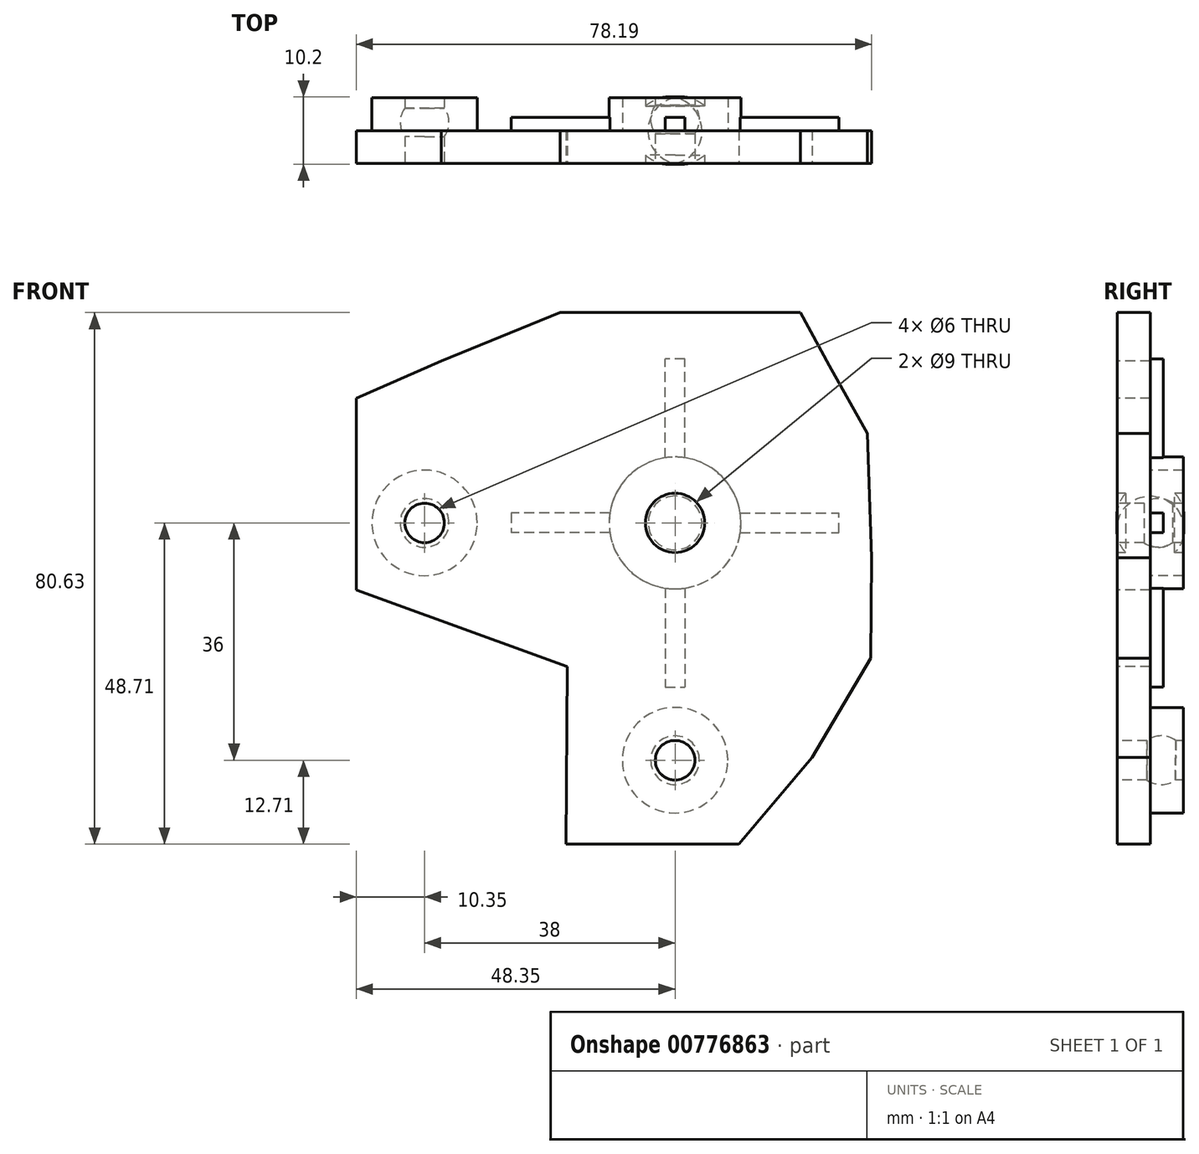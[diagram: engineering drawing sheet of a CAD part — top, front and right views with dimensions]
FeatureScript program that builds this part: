
annotation { "Feature Type Name" : "Feature", "Feature Type Description" : "" }
export const myFeature = defineFeature(function(context is Context, id is Id, definition is map)
    precondition{}
    {
        {
            var Q0;
            Q0=qCreatedBy(makeId("Front.planeOp"),FACE);
            var sketch = newSketch(context, id + "F0", { "sketchPlane" : qUnion([Q0])});
            skCircle(sketch, "E0", {"center": v(0, 0) * mm, "radius": 4.5 * mm});
            skCircle(sketch, "E1", {"center": v(-38, 0) * mm, "radius": 3 * mm});
            skCircle(sketch, "E2", {"center": v(0, -36) * mm, "radius": 3 * mm});
            skCircle(sketch, "E3", {"center": v(0, 0) * mm, "radius": 10 * mm});
            skCircle(sketch, "E4.0", {"center": v(-38, 0) * mm, "radius": 8 * mm});
            skCircle(sketch, "E5.0", {"center": v(0, -36) * mm, "radius": 8 * mm});
            skLineSegment(sketch, "E6", {"start": v(0, 29.34) * mm, "end": v(0, -69.9) * mm, "construction": true});
            skLineSegment(sketch, "E7", {"start": v(-65.38, 0) * mm, "end": v(35.9, 0) * mm, "construction": true});
            skLineSegment(sketch, "E8", {"start": v(-17.46, 31.92) * mm, "end": v(-35.49, 24.56) * mm});
            skLineSegment(sketch, "E9", {"start": v(-48.35, 18.9) * mm, "end": v(-35.49, 24.56) * mm});
            skLineSegment(sketch, "E10", {"start": v(-48.35, 18.9) * mm, "end": v(-48.35, -10.17) * mm});
            skLineSegment(sketch, "E11", {"start": v(-48.35, -10.17) * mm, "end": v(-16.38, -21.8) * mm});
            skLineSegment(sketch, "E12", {"start": v(-16.57, -48.71) * mm, "end": v(-16.38, -21.8) * mm});
            skLineSegment(sketch, "E13", {"start": v(-16.57, -48.71) * mm, "end": v(9.71, -48.71) * mm});
            skLineSegment(sketch, "E14", {"start": v(9.71, -48.71) * mm, "end": v(20.77, -35.57) * mm});
            skLineSegment(sketch, "E15", {"start": v(20.77, -35.57) * mm, "end": v(29.67, -20.52) * mm});
            skLineSegment(sketch, "E16", {"start": v(29.67, -20.52) * mm, "end": v(29.84, -5.25) * mm});
            skLineSegment(sketch, "E17", {"start": v(29.84, -5.25) * mm, "end": v(29.15, 13.57) * mm});
            skLineSegment(sketch, "E18", {"start": v(29.15, 13.57) * mm, "end": v(23.42, 23.88) * mm});
            skLineSegment(sketch, "E19", {"start": v(23.42, 23.88) * mm, "end": v(19, 31.92) * mm});
            skLineSegment(sketch, "E20", {"start": v(19, 31.92) * mm, "end": v(-17.46, 31.92) * mm});
            skLineSegment(sketch, "E21", {"start": v(-1.5, 9.89) * mm, "end": v(-1.5, 24.89) * mm});
            skLineSegment(sketch, "E22", {"start": v(-1.5, 24.89) * mm, "end": v(0, 24.89) * mm});
            skLineSegment(sketch, "E23.MirrorCS", {"start": v(1.5, 9.89) * mm, "end": v(1.5, 24.89) * mm});
            skLineSegment(sketch, "E24.MirrorCS", {"start": v(1.5, 24.89) * mm, "end": v(0, 24.89) * mm});
            skLineSegment(sketch, "E25.MirrorCS", {"start": v(1.5, -24.89) * mm, "end": v(0, -24.89) * mm});
            skLineSegment(sketch, "E26.MirrorCS", {"start": v(1.5, -9.89) * mm, "end": v(1.5, -24.89) * mm});
            skLineSegment(sketch, "E27.MirrorCS", {"start": v(-1.5, -9.89) * mm, "end": v(-1.5, -24.89) * mm});
            skLineSegment(sketch, "E28.MirrorCS", {"start": v(-1.5, -24.89) * mm, "end": v(0, -24.89) * mm});
            skLineSegment(sketch, "E29", {"start": v(9.89, 1.5) * mm, "end": v(24.89, 1.5) * mm});
            skLineSegment(sketch, "E30", {"start": v(24.89, 1.5) * mm, "end": v(24.89, 0) * mm});
            skLineSegment(sketch, "E31.MirrorCS", {"start": v(9.89, -1.5) * mm, "end": v(24.89, -1.5) * mm});
            skLineSegment(sketch, "E32.MirrorCS", {"start": v(24.89, -1.5) * mm, "end": v(24.89, 0) * mm});
            skLineSegment(sketch, "E33.MirrorCS", {"start": v(-24.89, -1.5) * mm, "end": v(-24.89, 0) * mm});
            skLineSegment(sketch, "E34.MirrorCS", {"start": v(-24.89, 1.5) * mm, "end": v(-24.89, 0) * mm});
            skLineSegment(sketch, "E35.MirrorCS", {"start": v(-9.89, 1.5) * mm, "end": v(-24.89, 1.5) * mm});
            skLineSegment(sketch, "E36.MirrorCS", {"start": v(-9.89, -1.5) * mm, "end": v(-24.89, -1.5) * mm});
            skSolve(sketch);
        }
        {
            var Q0;
            Q0=makeQuery(id+"F0.imprint","IMPRINT",FACE,{"disambiguationData":[TD([[makeQuery(id+"F0.imprint","IMPRINT",EDGE,{"derivedFrom":sQuery(id+"F0.wireOp",EDGE,"E3")}),-1.0]])]});
            var Q1;
            Q1=makeQuery(id+"F0.imprint","IMPRINT",FACE,{"disambiguationData":[TD([[makeQuery(id+"F0.imprint","IMPRINT",EDGE,{"derivedFrom":sQuery(id+"F0.wireOp",EDGE,"E0")}),-1.0]])]});
            var Q2;
            Q2=makeQuery(id+"F0.imprint","IMPRINT",FACE,{"disambiguationData":[TD([[makeQuery(id+"F0.imprint","IMPRINT",EDGE,{"derivedFrom":sQuery(id+"F0.wireOp",EDGE,"E1")}),-1.0]])]});
            var Q3;
            Q3=makeQuery(id+"F0.imprint","IMPRINT",FACE,{"disambiguationData":[TD([[makeQuery(id+"F0.imprint","IMPRINT",EDGE,{"derivedFrom":sQuery(id+"F0.wireOp",EDGE,"E2")}),-1.0]])]});
            var Q4;
            Q4=makeQuery(id+"F0.imprint","IMPRINT",FACE,{"disambiguationData":[TD([[makeQuery(id+"F0.imprint","IMPRINT",EDGE,{"derivedFrom":sQuery(id+"F0.wireOp",EDGE,"E33.MirrorCS")}),-1.0]])]});
            var Q5;
            {var subQ1=sQuery(id+"F0.wireOp",EDGE,"E21");Q5=makeQuery(id+"F0.imprint","IMPRINT",FACE,{"disambiguationData":[TD([[makeQuery(id+"F0.imprint","IMPRINT",EDGE,{"derivedFrom":subQ1}),-1.0]])]});}
            var Q6;
            {var subQ0=sQuery(id+"F0.wireOp",EDGE,"E29");Q6=makeQuery(id+"F0.imprint","IMPRINT",FACE,{"disambiguationData":[TD([[makeQuery(id+"F0.imprint","IMPRINT",EDGE,{"derivedFrom":subQ0}),-1.0]])]});}
            var Q7;
            Q7=makeQuery(id+"F0.imprint","IMPRINT",FACE,{"disambiguationData":[TD([[makeQuery(id+"F0.imprint","IMPRINT",EDGE,{"derivedFrom":sQuery(id+"F0.wireOp",EDGE,"E25.MirrorCS")}),-1.0]])]});
            extrude(context, id + "F1", {"entities" : qUnion([Q0, Q1, Q2, Q3, Q4, Q5, Q6, Q7]), "depth" : -5 * mm, "offsetDistance" : 25 * mm});
        }
        {
            var Q0;
            Q0=makeQuery(id+"F0.imprint","IMPRINT",FACE,{"disambiguationData":[TD([[makeQuery(id+"F0.imprint","IMPRINT",EDGE,{"derivedFrom":sQuery(id+"F0.wireOp",EDGE,"E0")}),-1.0]])]});
            var Q1;
            Q1=makeQuery(id+"F0.imprint","IMPRINT",FACE,{"disambiguationData":[TD([[makeQuery(id+"F0.imprint","IMPRINT",EDGE,{"derivedFrom":sQuery(id+"F0.wireOp",EDGE,"E2")}),-1.0]])]});
            var Q2;
            Q2=makeQuery(id+"F0.imprint","IMPRINT",FACE,{"disambiguationData":[TD([[makeQuery(id+"F0.imprint","IMPRINT",EDGE,{"derivedFrom":sQuery(id+"F0.wireOp",EDGE,"E1")}),-1.0]])]});
            extrude(context, id + "F2", {"entities" : qUnion([Q0, Q1, Q2]), "operationType" : NewBodyOperationType.ADD, "depth" : -10 * mm, "offsetDistance" : 25 * mm});
        }
        {
            var Q0;
            Q0=makeQuery(id+"F0.imprint","IMPRINT",FACE,{"disambiguationData":[TD([[makeQuery(id+"F0.imprint","IMPRINT",EDGE,{"derivedFrom":sQuery(id+"F0.wireOp",EDGE,"E33.MirrorCS")}),-1.0]])]});
            var Q1;
            Q1=makeQuery(id+"F0.imprint","IMPRINT",FACE,{"disambiguationData":[TD([[makeQuery(id+"F0.imprint","IMPRINT",EDGE,{"derivedFrom":sQuery(id+"F0.wireOp",EDGE,"E25.MirrorCS")}),-1.0]])]});
            var Q2;
            {var subQ0=sQuery(id+"F0.wireOp",EDGE,"E29");Q2=makeQuery(id+"F0.imprint","IMPRINT",FACE,{"disambiguationData":[TD([[makeQuery(id+"F0.imprint","IMPRINT",EDGE,{"derivedFrom":subQ0}),-1.0]])]});}
            var Q3;
            {var subQ1=sQuery(id+"F0.wireOp",EDGE,"E21");Q3=makeQuery(id+"F0.imprint","IMPRINT",FACE,{"disambiguationData":[TD([[makeQuery(id+"F0.imprint","IMPRINT",EDGE,{"derivedFrom":subQ1}),-1.0]])]});}
            extrude(context, id + "F3", {"entities" : qUnion([Q0, Q1, Q2, Q3]), "operationType" : NewBodyOperationType.ADD, "depth" : -7 * mm, "offsetDistance" : 25 * mm});
        }
        {
            var Q0;
            Q0=qCreatedBy(makeId("Right.planeOp"),FACE);
            var sketch = newSketch(context, id + "F4", { "sketchPlane" : qUnion([Q0])});
            skLineSegment(sketch, "E37", {"start": v(10, 0) * mm, "end": v(28.2, 0.02) * mm, "construction": true});
            skLineSegment(sketch, "E38.0", {"start": v(-21.9, -36.02) * mm, "end": v(28.17, -35.97) * mm, "construction": true});
            skPoint(sketch, "E39", {"position": v(10.38, -35.99) * mm});
            skLineSegment(sketch, "E40", {"start": v(10.38, -35.99) * mm, "end": v(2.98, -36) * mm});
            skArc(sketch, "E41", {"start": v(10.38, -35.99) * mm, "mid": v(6.68, -32.3) * mm, "end": v(2.98, -36) * mm});
            skPoint(sketch, "E42", {"position": v(0, -36) * mm});
            skPoint(sketch, "E43", {"position": v(20.1, 0.01) * mm});
            skLineSegment(sketch, "E44", {"start": v(10, 0) * mm, "end": v(0, 0) * mm});
            skArc(sketch, "E45", {"start": v(10, 0) * mm, "mid": v(5, 6.1) * mm, "end": v(0, 0) * mm});
            skSolve(sketch);
        }
        {
            var Q0;
            Q0=qCreatedBy(makeId("Top.planeOp"),FACE);
            var sketch = newSketch(context, id + "F5", { "sketchPlane" : qUnion([Q0])});
            skLineSegment(sketch, "E46", {"start": v(-38, 9.95) * mm, "end": v(-38, 0) * mm, "construction": true});
            skLineSegment(sketch, "E47", {"start": v(-38, 2.55) * mm, "end": v(-38, 9.95) * mm});
            skArc(sketch, "E48", {"start": v(-38, 9.95) * mm, "mid": v(-41.7, 6.25) * mm, "end": v(-38, 2.55) * mm});
            skPoint(sketch, "E49", {"position": v(-38, 4.97) * mm});
            skSolve(sketch);
        }
        {
            var Q0;
            Q0=makeQuery(id+"F5.imprint","IMPRINT",FACE,{"disambiguationData":[TD([[makeQuery(id+"F5.imprint","IMPRINT",EDGE,{"derivedFrom":sQuery(id+"F5.wireOp",EDGE,"E47")}),1.0]])]});
            var Q1;
            Q1=sQuery(id+"F5.wireOp",EDGE,"E46");
            revolve(context, id + "F6", {"operationType" : NewBodyOperationType.REMOVE, "surfaceOperationType" : NewSurfaceOperationType.NEW, "entities" : qUnion([Q0]), "axis" : qUnion([Q1]), "revolveType" : RevolveType.FULL, "oppositeDirection" : true});
        }
        {
            var Q0;
            Q0=makeQuery(id+"F4.imprint","IMPRINT",FACE,{"disambiguationData":[TD([[makeQuery(id+"F4.imprint","IMPRINT",EDGE,{"derivedFrom":sQuery(id+"F4.wireOp",EDGE,"E40")}),-1.0]])]});
            var Q1;
            Q1=sQuery(id+"F4.wireOp",EDGE,"E38.0");
            revolve(context, id + "F7", {"operationType" : NewBodyOperationType.REMOVE, "surfaceOperationType" : NewSurfaceOperationType.NEW, "entities" : qUnion([Q0]), "axis" : qUnion([Q1]), "revolveType" : RevolveType.FULL, "oppositeDirection" : true});
        }
        {
            var Q0;
            Q0=makeQuery(id+"F4.imprint","IMPRINT",FACE,{"disambiguationData":[TD([[makeQuery(id+"F4.imprint","IMPRINT",EDGE,{"derivedFrom":sQuery(id+"F4.wireOp",EDGE,"E44")}),-1.0]])]});
            var Q1;
            Q1=sQuery(id+"F4.wireOp",EDGE,"E44");
            revolve(context, id + "F8", {"operationType" : NewBodyOperationType.REMOVE, "surfaceOperationType" : NewSurfaceOperationType.NEW, "entities" : qUnion([Q0]), "axis" : qUnion([Q1]), "revolveType" : RevolveType.FULL, "oppositeDirection" : true});
        }
    });
